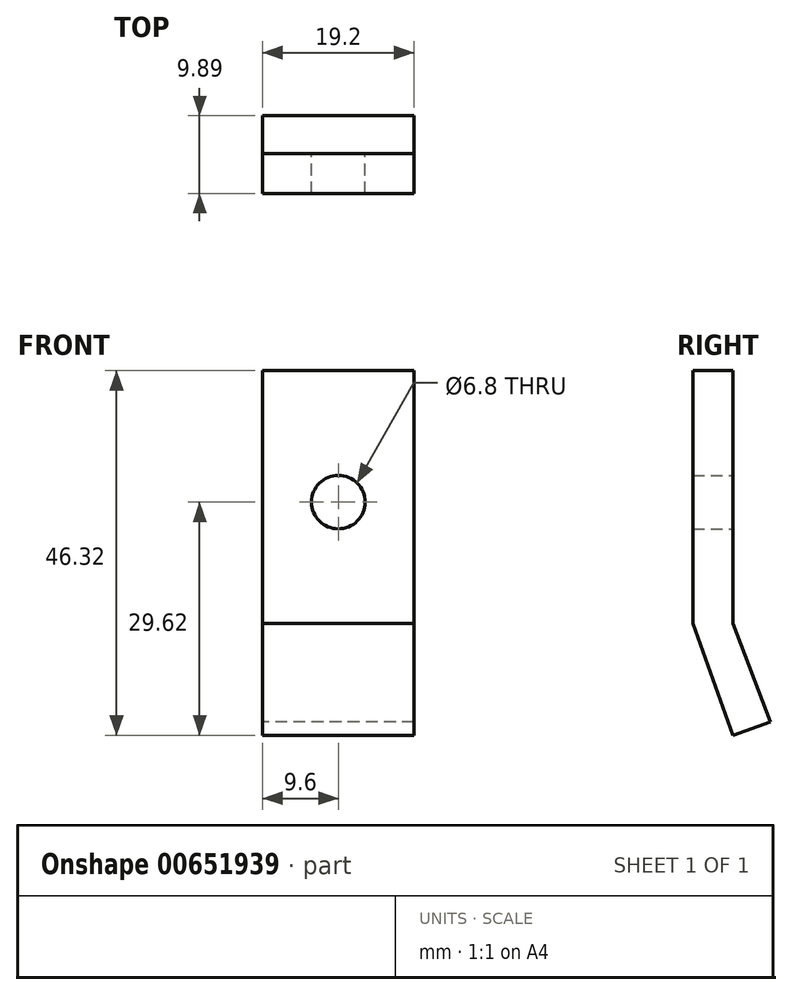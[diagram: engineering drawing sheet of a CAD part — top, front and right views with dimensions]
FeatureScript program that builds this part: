
annotation { "Feature Type Name" : "Feature", "Feature Type Description" : "" }
export const myFeature = defineFeature(function(context is Context, id is Id, definition is map)
    precondition{}
    {
        {
            var Q0;
            Q0=qCreatedBy(makeId("Right.planeOp"),FACE);
            var sketch = newSketch(context, id + "F0", { "sketchPlane" : qUnion([Q0])});
            skLineSegment(sketch, "E0.bottom", {"start": v(-2.55, 16.05) * mm, "end": v(2.55, 16.05) * mm});
            skLineSegment(sketch, "E0.top", {"start": v(-2.55, -16.05) * mm, "end": v(2.55, -16.05) * mm});
            skLineSegment(sketch, "E0.left", {"start": v(-2.55, 16.05) * mm, "end": v(-2.55, -16.05) * mm});
            skLineSegment(sketch, "E0.right", {"start": v(2.55, 16.05) * mm, "end": v(2.55, -16.05) * mm});
            skPoint(sketch, "E0.middle", {"position": v(0, 0) * mm});
            skLineSegment(sketch, "E1", {"start": v(-2.55, -16.05) * mm, "end": v(2.54, -30.27) * mm});
            skLineSegment(sketch, "E2", {"start": v(2.54, -30.27) * mm, "end": v(7.34, -28.55) * mm});
            skLineSegment(sketch, "E3", {"start": v(7.34, -28.55) * mm, "end": v(2.55, -16.05) * mm});
            skSolve(sketch);
        }
        {
            var Q0;
            Q0 = qSketchRegion(id + "F0", true);
            extrude(context, id + "F1", {"entities" : qUnion([Q0]), "depth" : 19.2 * mm, "offsetDistance" : 25.4 * mm});
        }
        {
            var Q0;
            Q0=makeQuery(id+"F1.opExtrude","SWEPT_FACE",FACE,{"disambiguationData":[OSD([sQuery(id+"F0.wireOp",EDGE,"E0.right")])]});
            var sketch = newSketch(context, id + "F2", { "sketchPlane" : qUnion([Q0])});
            skLineSegment(sketch, "E4", {"start": v(-9.6, 16.05) * mm, "end": v(-9.6, -0.65) * mm});
            skLineSegment(sketch, "E5", {"start": v(-19.2, -8.53) * mm, "end": v(-12.1, -8.53) * mm});
            skCircle(sketch, "E6", {"center": v(-9.6, -0.65) * mm, "radius": 3.4 * mm});
            skSolve(sketch);
        }
        {
            var Q0;
            Q0 = qSketchRegion(id + "F2", true);
            extrude(context, id + "F3", {"entities" : qUnion([Q0]), "operationType" : NewBodyOperationType.REMOVE, "endBound" : BoundingType.THROUGH_ALL, "oppositeDirection" : true, "depth" : 25.4 * mm, "offsetDistance" : 25.4 * mm});
        }
    });
